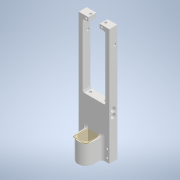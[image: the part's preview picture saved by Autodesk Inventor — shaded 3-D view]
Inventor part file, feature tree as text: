
AUTODESK INVENTOR PART (.ipt)
format: ipt  version: 2022 (Build 260153000, 153)  size: 265,216 bytes
history: native  units: in
note: dims shown in document units (in); Inventor stores cm internally (conversion verified against a paired STEP export)
features: extrude x5, sketch x5, other x4, plane x3, reference x3, fillet x1, projected_geometry x1
ambient origin geometry x8: Origin, YZ Plane, XZ Plane, XY Plane, X Axis, Y Axis, Z Axis, Center Point
bodies: Solid1 (feature_tree)
feature tree (22):
  extrude  "Extrusion1"  Depth=0.3937in TaperAngle=0.0deg
  sketch  "Sketch2"  dims[d13=0.1969in d14=0.1693in]
  plane  "Work Plane1"
  extrude  "Extrusion2"  Depth=0.1693in
  plane  "Work Plane2"
  extrude  "Extrusion4"  Depth=0.1969in
  extrude  "Extrusion5"  Depth=0.3937in TaperAngle=0.0deg
  plane  "Work Plane3"
  extrude  "Extrusion6"  Depth=1.9685in
  fillet  "Fillet2"  Radius=0.3937in
  sketch  "Sketch1"  dims[d0=0.0in d1=0.0in d2=0.3937in d3=0.0in]
  projected_geometry  "Projected Loop1"
  sketch  "Sketch5"  dims[d15=0.0in d16=0.0in d17=0.1969in]
  reference  "Reference5"
  reference  "Reference6"
  sketch  "Sketch6"  dims[d18=0.1969in d19=0.3937in d20=0.0in]
  sketch  "Sketch7"  dims[d21=0.0079in d22=0.1969in d23=0.3937in d24=0.0in d25=0.315in d4=0.0197in d5=1.9685in]
  reference  "Reference7"
  other  "Boss-Extrude11"
  other  "Linear Rail Assembly.iam"
  other  "Linear Rail Base:1"
  other  "linear actuator:1"
